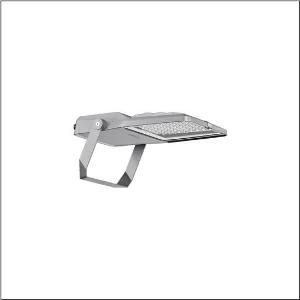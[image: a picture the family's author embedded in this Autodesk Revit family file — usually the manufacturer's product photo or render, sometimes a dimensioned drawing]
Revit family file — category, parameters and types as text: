
# Revit family: floodlight_fl_21_iq_mini___pl43_5xa7772c5a1a_be68
name_source: partatom
category: Lighting Fixtures
units: mm (PartAtom-declared; Revit-internal decimal feet)

## family parameters
Cut with Voids When Loaded = No
Host = Face
Light Source = No
Part Type = Normal
Room Calculation Point = No
Round Connector Dimension = Use Diameter
Shared = No

## types (1)
- --- (1 x LED, 11690 lm, 87.2 W, 4000K)
    Apparent Load = 87 VA
    CIE Flux Codes = 27 78 99 100 100
    Color Rendering = 80
    Color Temperature = 4000K
    Default Elevation = 1800 mm
    Description = Floodlight FL 21 iQ mini, floodlight, primary light control with lens, of PMMA, primary optical cover: protective disc, of toughened safety glass, transparent, light distribution: PL43, light emission: direct distribution, installation type: surface-mounted, LED, High Power LED, rated luminous flux: 11.690lm, luminous efficacy: 134lm/W, light colour: 840, colour temperature: 4000K, control: Street-Remote, Auto-Match, Temp-Guard, Night-Set, Smart-Wire, Desk-Remote (wireless, voltage-free reading and setting of iQ features in the workshop via application-optimized NFC function/RFID function), optimised constant luminous flux control (CLO 2.0), with terminal, 6-pole, mains connection: 220..240V, AC, 50/60Hz, start of lifetime: 87W, end of service life: 92W, reduction: 40W, luminaire housing, of diecast aluminium, powder-coated, Siteco® metallic grey (DB 702S), corrosivity category C5 mid according to DIN EN ISO 12944, sealing non-destructively replaceable, mounting bracket, of steel, galvanised, powder-coated, Siteco® metallic grey (DB 702S), protection rating (complete): IP66, insulation class (complete): insulation class II (safety insulation), certification: CE, ENEC, VDE, protection symbol: D, impact resistance: IK08, permissible operating ambient temperature: -40..+40°C, permissible operating ambient temperature for outdoor applications: -40..+50°C, standard: DIN EN 12944, LABS conformity tested according to VDMA 24364:2018-05, packaging unit: 1 piece

Light Distribution: PL43
    Height = 70 mm
    Lamp = 1 x LED
    Lamp Light Flux = 11690 lm
    Lamp Power = 87.2 W
    Lamp count = 1
    Length = 485 mm
    Luminous efficacy = 134 lm/W
    Manufacturer = Siteco
    ModVariant = No
    Model = 5XA7772C5A1A
    Number of Poles = 1
    OnlyDefault = Yes
    Power Factor = 1
    Product Name = Floodlight FL 21 iQ mini | PL43
    Product group = floodlight | pylon annexe
    ProductGroupID = 6200
    Protection Class = Protection class II
    Protection Degree = IP 66
    RLX_Detail_Level = 1
    RLX_Emergency_Light_Flux = 0 lm
    RLX_Emergency_Type = 0
    RLX_Emergency_Type_DB = No
    RlxData = <blob elided: 96037 chars, md5=16bbb988>
    Socket = socket
    Standby Power = 0 W
    System Light Flux = 11690 lm
    System Power = 87 W
    Type Comments = factory setting: luminous flux: 100 % | dim-lin: 254 | 456 mA
    Type Image = l_1006845.jpg
    URL = http://relux.com
    VarID = @adj_094425
    Voltage = 0 V
    Weight = 0.00 kg
    Width = 337 mm

## geometry (parser evidence)
native form markers: Blend x4, Sweep x12
no freeform markers — native parametric forms only
